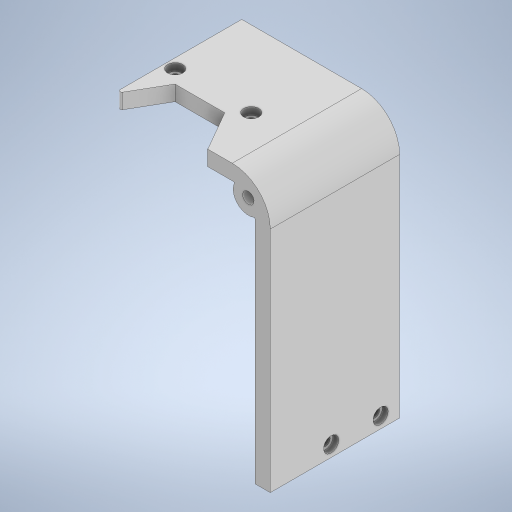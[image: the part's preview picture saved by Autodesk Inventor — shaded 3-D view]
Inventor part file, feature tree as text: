
AUTODESK INVENTOR PART (.ipt)
format: ipt  version: 2023.1 (Build 271208000, 208)  size: 327,168 bytes
history: native  units: mm
features: extrude x10, sketch x8, other x1, fillet x1, projected_geometry x1
ambient origin geometry x8: Origin, YZ Plane, XZ Plane, XY Plane, X Axis, Y Axis, Z Axis, Center Point
bodies: Body1 (feature_tree)
feature tree (21):
  other  "솔리드1"
  extrude  "돌출1"  Depth=70.0mm
  extrude  "돌출2"  Depth=41.5mm
  extrude  "돌출3"  Depth=4.0mm
  extrude  "돌출4"  TaperAngle=90.0deg  [1 undecoded]
  extrude  "돌출5"  Depth=6.0mm
  fillet  "모깎기2"  Radius=10.0mm
  sketch  "스케치6"
  extrude  "돌출6"  Depth=23.0mm TaperAngle=0.0deg
  extrude  "돌출7"  Depth=6.0mm
  sketch  "스케치7"
  extrude  "돌출8"  Depth=2.5mm
  extrude  "돌출9"  Depth=2.5mm
  extrude  "돌출10"  Depth=5.0mm
  sketch  "스케치1"
  sketch  "스케치2"
  sketch  "스케치3"
  sketch  "스케치4"
  sketch  "스케치5"
  projected_geometry  "투영된 루프1"
  sketch  "스케치8"
note: 1 required parameter value undecoded (feature->parameter linkage not recoverable at this tier; creation-order binding heuristic only, values carry confidence <= 0.55)
